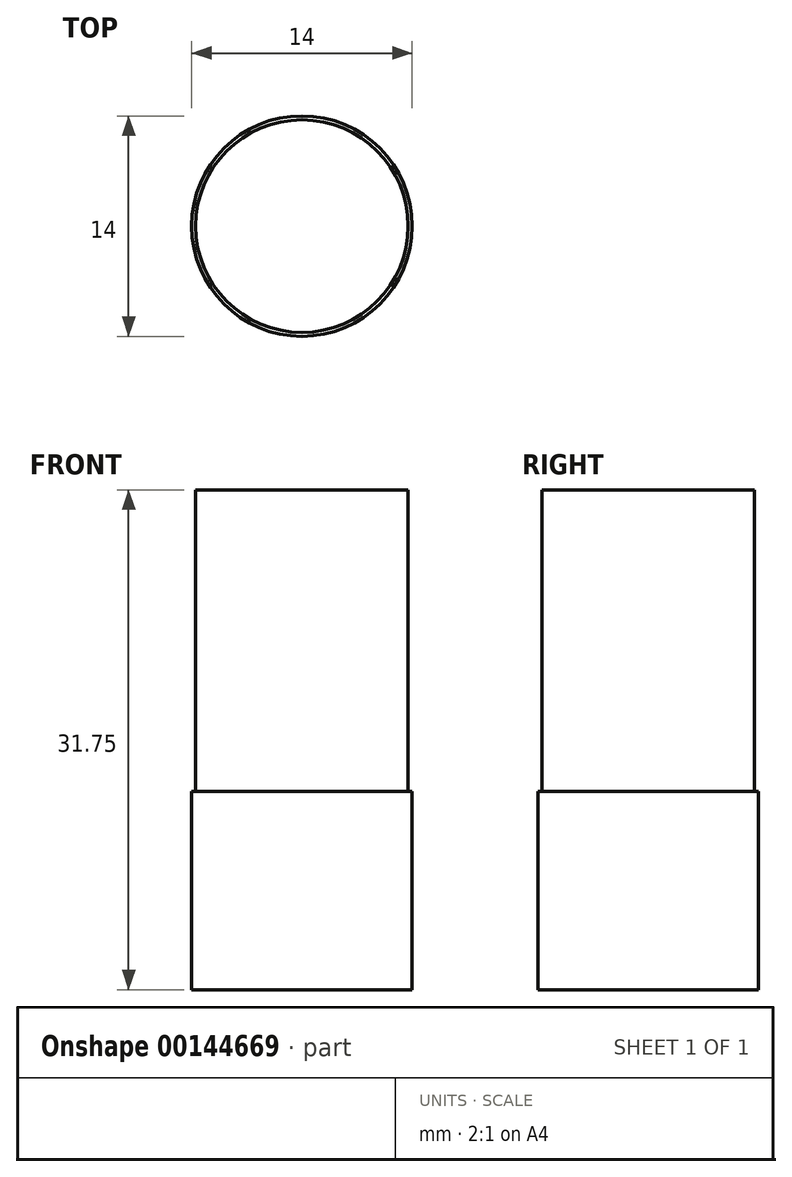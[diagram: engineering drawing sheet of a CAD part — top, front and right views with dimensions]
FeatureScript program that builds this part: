
annotation { "Feature Type Name" : "Feature", "Feature Type Description" : "" }
export const myFeature = defineFeature(function(context is Context, id is Id, definition is map)
    precondition{}
    {
        {
            var Q0;
            Q0=qCreatedBy(makeId("Top.planeOp"),FACE);
            var sketch = newSketch(context, id + "F0", { "sketchPlane" : qUnion([Q0])});
            skCircle(sketch, "E0", {"center": v(0, 0) * mm, "radius": 7 * mm});
            skCircle(sketch, "E1", {"center": v(0, 0) * mm, "radius": 6.75 * mm});
            skSolve(sketch);
        }
        {
            var Q0;
            Q0=makeQuery(id+"F0.imprint","IMPRINT",FACE,{"disambiguationData":[TD([[makeQuery(id+"F0.imprint","IMPRINT",EDGE,{"derivedFrom":sQuery(id+"F0.wireOp",EDGE,"E0")}),1.0]])]});
            var Q1;
            Q1=makeQuery(id+"F0.imprint","IMPRINT",FACE,{"disambiguationData":[TD([[makeQuery(id+"F0.imprint","IMPRINT",EDGE,{"derivedFrom":sQuery(id+"F0.wireOp",EDGE,"E1")}),1.0]])]});
            extrude(context, id + "F1", {"entities" : qUnion([Q0, Q1]), "oppositeDirection" : true, "depth" : 12.6 * mm});
        }
        {
            var Q0;
            Q0=makeQuery(id+"F0.imprint","IMPRINT",FACE,{"disambiguationData":[TD([[makeQuery(id+"F0.imprint","IMPRINT",EDGE,{"derivedFrom":sQuery(id+"F0.wireOp",EDGE,"E1")}),1.0]])]});
            extrude(context, id + "F2", {"entities" : qUnion([Q0]), "operationType" : NewBodyOperationType.ADD, "depth" : (31.75 - 12.6) * mm});
        }
    });
